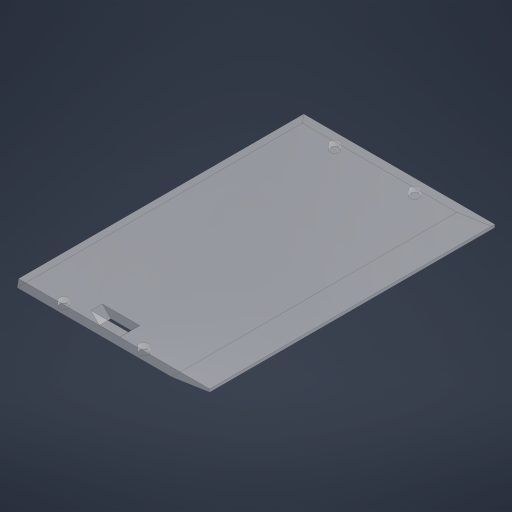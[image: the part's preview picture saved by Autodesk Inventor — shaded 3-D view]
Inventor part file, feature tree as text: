
AUTODESK INVENTOR PART (.ipt)
format: ipt  version: 2024 (Build 280153000, 153)  size: 222,208 bytes
history: native  units: in
note: dims shown in document units (in); Inventor stores cm internally (conversion verified against a paired STEP export)
features: extrude x3, sketch x3, chamfer x1
ambient origin geometry x8: Origin, YZ Plane, XZ Plane, XY Plane, X Axis, Y Axis, Z Axis, Center Point
bodies: Solid1 (feature_tree)
feature tree (7):
  extrude  "Extrusion1"  Depth=3.937in TaperAngle=0.0deg
  extrude  "Extrusion2"  Depth=0.1181in TaperAngle=45.0deg
  chamfer  "Chamfer2"  Distance=0.0394in
  extrude  "Extrusion3"  Depth=0.1181in
  sketch  "Sketch1"  dims[d0=2.6378in d1=3.937in d2=0.0in]
  sketch  "Sketch3"  dims[d21=0.0in d22=0.0in d23=0.1181in d24=0.0787in d25=45.0deg]
  sketch  "Sketch4"  dims[d26=0.1181in d27=0.0394in d28=0.1181in d29=0.1181in d30=0.1181in d31=0.1181in d32=0.0984in d33=0.0984in d34=0.0984in d35=0.0984in d36=0.5467in d37=1.1024in d38=0.5467in d39=1.1024in d40=0.0787in d41=0.0in d46=0.0192in d48=0.5231in d49=1.0168in d50=0.2815in]
